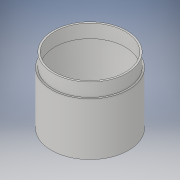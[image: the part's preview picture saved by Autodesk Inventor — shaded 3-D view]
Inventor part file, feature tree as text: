
AUTODESK INVENTOR PART (.ipt)
format: ipt  version: 2017 SP1 (Build 210196100, 196)  size: 160,768 bytes
history: native  units: in
note: dims shown in document units (in); Inventor stores cm internally (conversion verified against a paired STEP export)
features: revolve x1, sketch x1
ambient origin geometry x8: Origin, YZ Plane, XZ Plane, XY Plane, X Axis, Y Axis, Z Axis, Center Point
bodies: Solid1 (feature_tree)
feature tree (2):
  revolve  "Revolution1"  [1 undecoded]
  sketch  "Sketch1"  dims[d0=0.5in d1=1.13in d3=15.0deg d4=0.25in d9=1.5in d11=0.5in d13=3.75in d14=0.25in d15=1.0in d16=0.25in d17=0.5in d18=0.234in d19=0.234in d20=0.5in d22=4.25in d23=2.5in d25=1.0in d26=0.25in d27=5.25in d28=0.125in d29=4.0in d30=0.25in d31=0.1718in d32=1.75in d33=0.125in d34=0.801in d35=0.375in d37=90.0deg]
note: 1 required parameter value undecoded (feature->parameter linkage not recoverable at this tier; creation-order binding heuristic only, values carry confidence <= 0.55)
